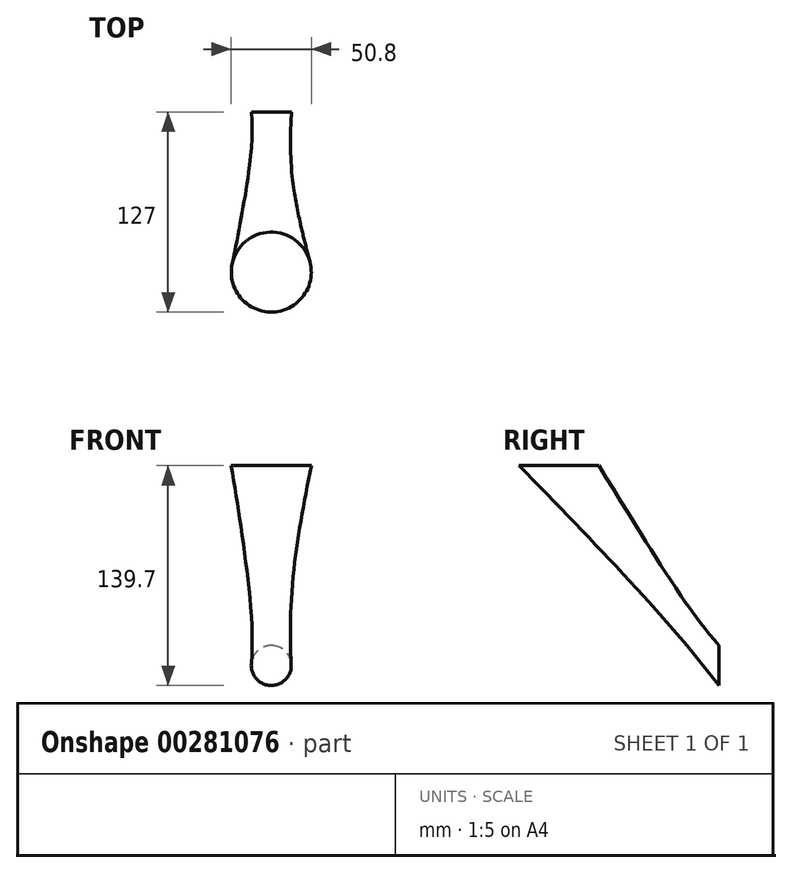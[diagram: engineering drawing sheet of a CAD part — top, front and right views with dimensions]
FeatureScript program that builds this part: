
annotation { "Feature Type Name" : "Feature", "Feature Type Description" : "" }
export const myFeature = defineFeature(function(context is Context, id is Id, definition is map)
    precondition{}
    {
        {
            var Q0;
            Q0=qCreatedBy(makeId("Front.planeOp"),FACE);
            var sketch = newSketch(context, id + "F0", { "sketchPlane" : qUnion([Q0])});
            skCircle(sketch, "E0", {"center": v(0, 0) * mm, "radius": 12.7 * mm});
            skSolve(sketch);
        }
        {
            var Q0;
            Q0=qCreatedBy(makeId("Top.planeOp"),FACE);
            cPlane(context, id + "F1", {"entities" : qUnion([Q0]), "cplaneType" : CPlaneType.OFFSET, "offset" : 127 * mm, "width" : 152.4 * mm, "height" : 152.4 * mm});
        }
        {
            var Q0;
            Q0=qCreatedBy(id+"F1.planeOp",FACE);
            var sketch = newSketch(context, id + "F2", { "sketchPlane" : qUnion([Q0])});
            skCircle(sketch, "E1", {"center": v(0, -101.6) * mm, "radius": 25.4 * mm});
            skSolve(sketch);
        }
        {
            var Q0;
            Q0=makeQuery(id+"F2.imprint","IMPRINT",FACE,{"disambiguationData":[TD([[makeQuery(id+"F2.imprint","IMPRINT",EDGE,{"derivedFrom":sQuery(id+"F2.wireOp",EDGE,"E1")}),1.0]])]});
            var Q1;
            Q1=makeQuery(id+"F0.imprint","IMPRINT",FACE,{"disambiguationData":[TD([[makeQuery(id+"F0.imprint","IMPRINT",EDGE,{"derivedFrom":sQuery(id+"F0.wireOp",EDGE,"E0")}),1.0]])]});
            loft(context, id + "F3", {"sheetProfilesArray" : [{ "sheetProfileEntities" : qUnion([Q0]) }, { "sheetProfileEntities" : qUnion([Q1]) }]});
        }
    });
